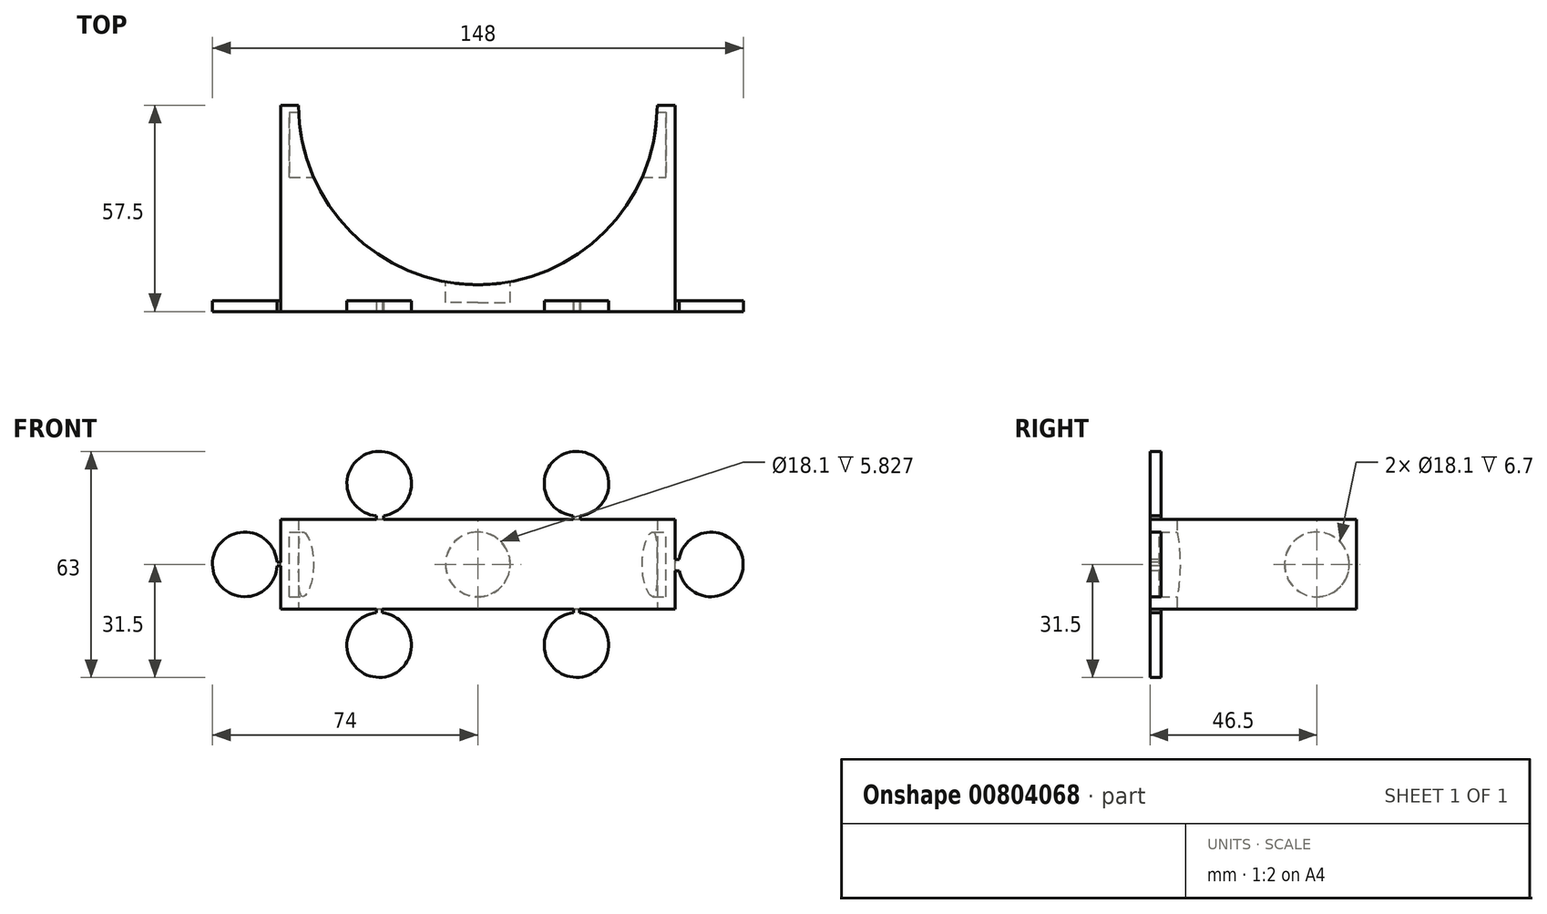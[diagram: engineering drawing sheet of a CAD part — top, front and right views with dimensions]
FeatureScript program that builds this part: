
annotation { "Feature Type Name" : "Feature", "Feature Type Description" : "" }
export const myFeature = defineFeature(function(context is Context, id is Id, definition is map)
    precondition{}
    {
        {
            var Q0;
            Q0=qCreatedBy(makeId("Top.planeOp"),FACE);
            var sketch = newSketch(context, id + "F0", { "sketchPlane" : qUnion([Q0])});
            skArc(sketch, "E0", {"start": v(-50, 0) * mm, "mid": v(0, -50) * mm, "end": v(50, 0) * mm});
            skArc(sketch, "E1", {"start": v(-55, 0) * mm, "mid": v(0, -55) * mm, "end": v(55, 0) * mm});
            skLineSegment(sketch, "E2", {"start": v(-55, 0) * mm, "end": v(-50, 0) * mm});
            skLineSegment(sketch, "E3.trimOffspring", {"start": v(50, 0) * mm, "end": v(55, 0) * mm});
            skSolve(sketch);
        }
        {
            var Q0;
            Q0=qSketchRegion(id+"F0",true);
            extrude(context, id + "F1", {"entities" : qUnion([Q0]), "endBound" : BoundingType.SYMMETRIC, "depth" : 25 * mm, "offsetDistance" : 25 * mm});
        }
        {
            var Q0;
            Q0=makeQuery(id+"F1.opExtrude","CAP_FACE",FACE,{"disambiguationData":[OSD([sQuery(id+"F0.wireOp",EDGE,"E0"),sQuery(id+"F0.wireOp",EDGE,"E1")])],"isStart":false});
            var sketch = newSketch(context, id + "F2", { "sketchPlane" : qUnion([Q0])});
            skLineSegment(sketch, "E4", {"start": v(-55, 0) * mm, "end": v(-55, -57.5) * mm});
            skLineSegment(sketch, "E5", {"start": v(55, 0) * mm, "end": v(55, -57.5) * mm});
            skLineSegment(sketch, "E6", {"start": v(0, -57.5) * mm, "end": v(55, -57.5) * mm});
            skLineSegment(sketch, "E7", {"start": v(0, -57.5) * mm, "end": v(-55, -57.5) * mm});
            skArc(sketch, "E8", {"start": v(-55, 0) * mm, "mid": v(0, -55) * mm, "end": v(55, 0) * mm});
            skLineSegment(sketch, "E9", {"start": v(0, -55) * mm, "end": v(0, -57.5) * mm, "construction": true});
            skSolve(sketch);
        }
        {
            var Q0;
            Q0=qSketchRegion(id+"F2",true);
            extrude(context, id + "F3", {"entities" : qUnion([Q0]), "operationType" : NewBodyOperationType.ADD, "oppositeDirection" : true, "depth" : 25 * mm, "offsetDistance" : 25 * mm});
        }
        {
            var Q0;
            Q0=qCreatedBy(makeId("Front.planeOp"),FACE);
            var sketch = newSketch(context, id + "F4", { "sketchPlane" : qUnion([Q0])});
            skCircle(sketch, "E10", {"center": v(0, 0) * mm, "radius": 9.05 * mm});
            skSolve(sketch);
        }
        {
            var Q0;
            Q0 = qSketchRegion(id + "F4", true);
            extrude(context, id + "F5", {"entities" : qUnion([Q0]), "operationType" : NewBodyOperationType.REMOVE, "depth" : 55 * mm, "offsetDistance" : 25 * mm});
        }
        {
            var Q0;
            Q0=qCreatedBy(makeId("Right.planeOp"),FACE);
            var sketch = newSketch(context, id + "F6", { "sketchPlane" : qUnion([Q0])});
            skLineSegment(sketch, "E11", {"start": v(0, 0) * mm, "end": v(-11, 0) * mm, "construction": true});
            skCircle(sketch, "E12", {"center": v(-11, 0) * mm, "radius": 9.05 * mm});
            skSolve(sketch);
        }
        {
            var Q0;
            Q0 = qSketchRegion(id + "F6", true);
            extrude(context, id + "F7", {"entities" : qUnion([Q0]), "operationType" : NewBodyOperationType.REMOVE, "endBound" : BoundingType.SYMMETRIC, "oppositeDirection" : true, "depth" : 105 * mm, "offsetDistance" : 25 * mm});
        }
        {
            var Q0;
            Q0=makeQuery(id+"F3.opExtrude","SWEPT_FACE",FACE,{"disambiguationData":[OSD([sQuery(id+"F2.wireOp",EDGE,"E6"),sQuery(id+"F2.wireOp",EDGE,"E7")])]});
            var sketch = newSketch(context, id + "F8", { "sketchPlane" : qUnion([Q0])});
            skLineSegment(sketch, "E13", {"start": v(55, 0) * mm, "end": v(65, 0) * mm, "construction": true});
            skLineSegment(sketch, "E14", {"start": v(-55, 0) * mm, "end": v(-65, 0) * mm, "construction": true});
            skArc(sketch, "E15", {"start": v(56.19, -1.83) * mm, "mid": v(74, 0.24) * mm, "end": v(56.1, 1.35) * mm});
            skArc(sketch, "E16", {"start": v(-56.02, 0.59) * mm, "mid": v(-74, -0.07) * mm, "end": v(-56.01, -0.44) * mm});
            skLineSegment(sketch, "E17", {"start": v(0, -12.5) * mm, "end": v(-55, -12.5) * mm, "construction": true});
            skLineSegment(sketch, "E18", {"start": v(-27.5, -12.5) * mm, "end": v(-27.5, -22.5) * mm, "construction": true});
            skLineSegment(sketch, "E19", {"start": v(0, -12.5) * mm, "end": v(55, -12.5) * mm, "construction": true});
            skLineSegment(sketch, "E20", {"start": v(27.5, -12.5) * mm, "end": v(27.5, -22.5) * mm, "construction": true});
            skLineSegment(sketch, "E21", {"start": v(-55, 12.5) * mm, "end": v(0, 12.5) * mm, "construction": true});
            skLineSegment(sketch, "E22", {"start": v(-27.5, 12.5) * mm, "end": v(-27.5, 22.5) * mm, "construction": true});
            skLineSegment(sketch, "E23", {"start": v(0, 12.5) * mm, "end": v(55, 12.5) * mm, "construction": true});
            skLineSegment(sketch, "E24", {"start": v(27.5, 12.5) * mm, "end": v(27.5, 22.5) * mm, "construction": true});
            skArc(sketch, "E25", {"start": v(26.67, -13.54) * mm, "mid": v(27.5, -31.5) * mm, "end": v(28.35, -13.54) * mm});
            skArc(sketch, "E26", {"start": v(-28.3, -13.54) * mm, "mid": v(-27.52, -31.5) * mm, "end": v(-26.66, -13.54) * mm});
            skArc(sketch, "E27", {"start": v(-26.33, 13.58) * mm, "mid": v(-27.67, 31.5) * mm, "end": v(-28.34, 13.54) * mm});
            skArc(sketch, "E28", {"start": v(28.64, 13.57) * mm, "mid": v(27.37, 31.5) * mm, "end": v(26.62, 13.54) * mm});
            skLineSegment(sketch, "E29", {"start": v(56.19, -1.83) * mm, "end": v(55, -1.83) * mm});
            skLineSegment(sketch, "E30", {"start": v(56.1, 1.35) * mm, "end": v(55, 1.35) * mm});
            skLineSegment(sketch, "E31", {"start": v(55, -1.83) * mm, "end": v(55, 1.35) * mm});
            skLineSegment(sketch, "E32", {"start": v(26.62, 13.54) * mm, "end": v(26.62, 12.5) * mm});
            skLineSegment(sketch, "E33", {"start": v(28.64, 13.57) * mm, "end": v(28.64, 12.5) * mm});
            skLineSegment(sketch, "E34", {"start": v(28.64, 12.5) * mm, "end": v(26.62, 12.5) * mm});
            skLineSegment(sketch, "E35", {"start": v(-28.34, 13.54) * mm, "end": v(-28.34, 12.5) * mm});
            skLineSegment(sketch, "E36", {"start": v(-26.33, 13.58) * mm, "end": v(-26.33, 12.5) * mm});
            skLineSegment(sketch, "E37", {"start": v(-26.33, 12.5) * mm, "end": v(-28.34, 12.5) * mm});
            skLineSegment(sketch, "E38", {"start": v(-56.02, 0.59) * mm, "end": v(-55, 0.59) * mm});
            skLineSegment(sketch, "E39", {"start": v(-56.01, -0.44) * mm, "end": v(-55, -0.44) * mm});
            skLineSegment(sketch, "E40", {"start": v(-55, -0.44) * mm, "end": v(-55, 0.59) * mm});
            skLineSegment(sketch, "E41", {"start": v(-28.3, -13.54) * mm, "end": v(-28.3, -12.5) * mm});
            skLineSegment(sketch, "E42", {"start": v(-26.66, -13.54) * mm, "end": v(-26.66, -12.5) * mm});
            skLineSegment(sketch, "E43", {"start": v(-26.66, -12.5) * mm, "end": v(-28.3, -12.5) * mm});
            skLineSegment(sketch, "E44", {"start": v(26.67, -13.54) * mm, "end": v(26.67, -12.5) * mm});
            skLineSegment(sketch, "E45", {"start": v(28.35, -13.54) * mm, "end": v(28.35, -12.5) * mm});
            skLineSegment(sketch, "E46", {"start": v(28.35, -12.5) * mm, "end": v(26.67, -12.5) * mm});
            skSolve(sketch);
        }
        {
            var Q0;
            Q0 = qSketchRegion(id + "F8", true);
            extrude(context, id + "F9", {"entities" : qUnion([Q0]), "operationType" : NewBodyOperationType.ADD, "oppositeDirection" : true, "depth" : 3 * mm, "offsetDistance" : 25 * mm});
        }
    });
